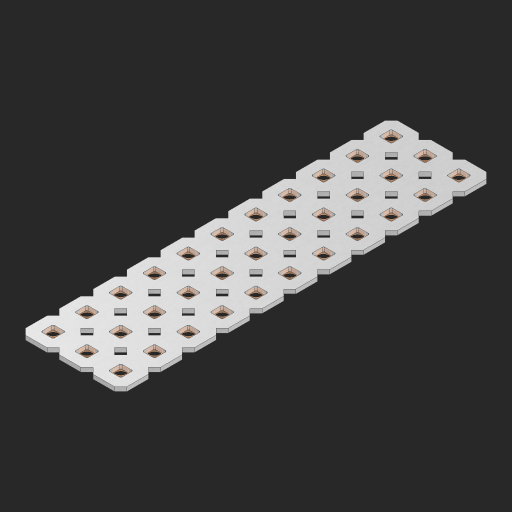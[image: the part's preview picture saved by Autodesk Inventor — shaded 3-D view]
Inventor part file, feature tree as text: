
AUTODESK INVENTOR PART (.ipt)
format: ipt  version: 2023 (Build 270158000, 158)  size: 668,160 bytes
history: native  units: in
note: dims shown in document units (in); Inventor stores cm internally (conversion verified against a paired STEP export)
features: other x34, extrude x32, sketch x2, pattern_linear x1
ambient origin geometry x8: Origin, YZ Plane, XZ Plane, XY Plane, X Axis, Y Axis, Z Axis, Center Point
bodies: Solid1 (feature_tree), Body (feature_tree)
feature tree (69):
  pattern_linear  "Rectangular Pattern1"  Spacing1=0.09in  [1 undecoded]
  sketch  "Sketch1"  dims[d1=0.5in]
  sketch  "Sketch2"  dims[d2=0.182in d3=0.09in d4=0.09in d5=0.09in d6=0.09in d7=0.09in d8=0.09in d9=0.09in d10=0.09in d11=0.02in d13=0.0in d14=0.172in d15=0.0625in d16=0.0in d19=0.5in d22=0.5in]
  other  "Srf1"
  other  "Srf126"
  other  "Srf127"
  other  "Srf128"
  other  "Srf129"
  other  "Srf130"
  other  "Srf131"
  other  "Srf250"
  other  "Srf251"
  other  "Srf252"
  other  "Srf253"
  other  "Srf268"
  other  "Srf269"
  other  "Srf270"
  other  "Srf271"
  other  "Srf272"
  other  "Srf273"
  other  "Srf274"
  other  "Srf275"
  other  "Srf276"
  other  "Srf277"
  other  "Srf278"
  other  "Srf293"
  other  "Srf294"
  other  "Srf295"
  other  "Srf296"
  other  "Srf297"
  other  "Srf298"
  other  "Srf299"
  other  "Srf300"
  other  "Srf301"
  other  "Srf302"
  other  "Srf303"
  other  "Circle"
  extrude  "ExtrusionSrf126"  Depth=0.09in
  extrude  "ExtrusionSrf127"  Depth=0.09in
  extrude  "ExtrusionSrf128"  Depth=0.09in
  extrude  "ExtrusionSrf129"  Depth=0.09in
  extrude  "ExtrusionSrf130"  Depth=0.09in
  extrude  "ExtrusionSrf131"  Depth=0.09in
  extrude  "ExtrusionSrf250"  Depth=0.09in
  extrude  "ExtrusionSrf251"  Depth=0.02in
  extrude  "ExtrusionSrf252"  TaperAngle=0.0deg  [1 undecoded]
  extrude  "ExtrusionSrf253"  Depth=0.5in
  extrude  "ExtrusionSrf268"  Depth=0.0625in TaperAngle=0.0deg
  extrude  "ExtrusionSrf269"  Depth=0.5in
  extrude  "ExtrusionSrf270"  Depth=0.5in
  extrude  "ExtrusionSrf271"  [1 undecoded]
  extrude  "ExtrusionSrf272"  [1 undecoded]
  extrude  "ExtrusionSrf273"  [1 undecoded]
  extrude  "ExtrusionSrf274"  [1 undecoded]
  extrude  "ExtrusionSrf275"  [1 undecoded]
  extrude  "ExtrusionSrf276"  [1 undecoded]
  extrude  "ExtrusionSrf277"  [1 undecoded]
  extrude  "ExtrusionSrf278"  [1 undecoded]
  extrude  "ExtrusionSrf293"  [1 undecoded]
  extrude  "ExtrusionSrf294"  [1 undecoded]
  extrude  "ExtrusionSrf295"  [1 undecoded]
  extrude  "ExtrusionSrf296"  [1 undecoded]
  extrude  "ExtrusionSrf297"  [1 undecoded]
  extrude  "ExtrusionSrf298"  [1 undecoded]
  extrude  "ExtrusionSrf299"  [1 undecoded]
  extrude  "ExtrusionSrf300"  [1 undecoded]
  extrude  "ExtrusionSrf301"  [1 undecoded]
  extrude  "ExtrusionSrf302"  [1 undecoded]
  extrude  "ExtrusionSrf303"  [1 undecoded]
note: 21 required parameter values undecoded (feature->parameter linkage not recoverable at this tier; creation-order binding heuristic only, values carry confidence <= 0.55)
